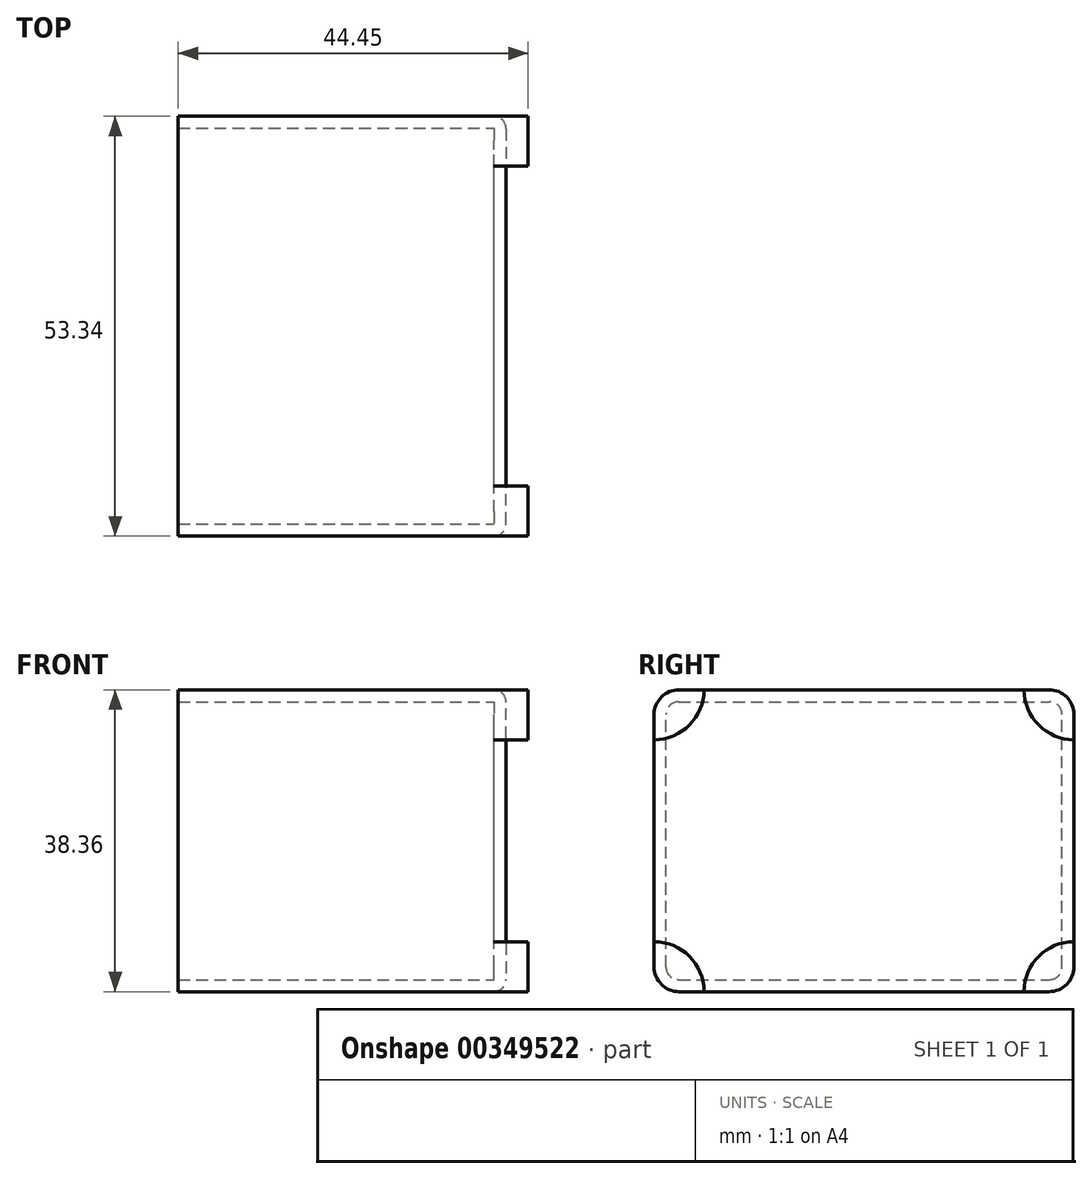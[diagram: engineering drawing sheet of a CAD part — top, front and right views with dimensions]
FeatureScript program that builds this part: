
annotation { "Feature Type Name" : "Feature", "Feature Type Description" : "" }
export const myFeature = defineFeature(function(context is Context, id is Id, definition is map)
    precondition{}
    {
        {
            var Q0;
            Q0=qCreatedBy(makeId("Right.planeOp"),FACE);
            var sketch = newSketch(context, id + "F0", { "sketchPlane" : qUnion([Q0])});
            skLineSegment(sketch, "E0.bottom", {"start": v(23.5, 19.18) * mm, "end": v(-23.5, 19.18) * mm});
            skLineSegment(sketch, "E0.top", {"start": v(23.5, -19.18) * mm, "end": v(-23.5, -19.18) * mm});
            skLineSegment(sketch, "E0.left", {"start": v(26.67, 16) * mm, "end": v(26.67, -16) * mm});
            skLineSegment(sketch, "E0.right", {"start": v(-26.67, 16) * mm, "end": v(-26.67, -16) * mm});
            skPoint(sketch, "E0.middle", {"position": v(0, 0) * mm});
            skPoint(sketch, "E1.visualSharp", {"position": v(-26.67, 19.18) * mm});
            skArc(sketch, "E1.filletArc", {"start": v(-23.5, 19.18) * mm, "mid": v(-25.74, 18.25) * mm, "end": v(-26.67, 16) * mm});
            skPoint(sketch, "E2.visualSharp", {"position": v(26.67, 19.18) * mm});
            skArc(sketch, "E2.filletArc", {"start": v(26.67, 16) * mm, "mid": v(25.74, 18.25) * mm, "end": v(23.5, 19.18) * mm});
            skPoint(sketch, "E3.visualSharp", {"position": v(26.67, -19.18) * mm});
            skArc(sketch, "E3.filletArc", {"start": v(23.5, -19.18) * mm, "mid": v(25.74, -18.25) * mm, "end": v(26.67, -16) * mm});
            skPoint(sketch, "E4.visualSharp", {"position": v(-26.67, -19.18) * mm});
            skArc(sketch, "E4.filletArc", {"start": v(-26.67, -16) * mm, "mid": v(-25.74, -18.25) * mm, "end": v(-23.5, -19.18) * mm});
            skSolve(sketch);
        }
        {
            var Q0;
            Q0 = qSketchRegion(id + "F0", true);
            extrude(context, id + "F1", {"entities" : qUnion([Q0]), "depth" : 1.52 * mm});
        }
        {
            var Q0;
            Q0=makeQuery(id+"F1.opExtrude","CAP_FACE",FACE,{"disambiguationData":[OSD([sQuery(id+"F0.wireOp",EDGE,"E0.bottom"),sQuery(id+"F0.wireOp",EDGE,"E0.top"),sQuery(id+"F0.wireOp",EDGE,"E0.left"),sQuery(id+"F0.wireOp",EDGE,"E0.right"),sQuery(id+"F0.wireOp",EDGE,"E1.filletArc"),sQuery(id+"F0.wireOp",EDGE,"E2.filletArc"),sQuery(id+"F0.wireOp",EDGE,"E3.filletArc"),sQuery(id+"F0.wireOp",EDGE,"E4.filletArc")])],"isStart":true});
            var sketch = newSketch(context, id + "F2", { "sketchPlane" : qUnion([Q0])});
            skPoint(sketch, "E5.middle", {"position": v(0, 0) * mm});
            skLineSegment(sketch, "E6.bottom", {"start": v(23.56, -17.65) * mm, "end": v(-23.56, -17.65) * mm});
            skLineSegment(sketch, "E6.top", {"start": v(23.56, 17.65) * mm, "end": v(-23.56, 17.65) * mm});
            skLineSegment(sketch, "E6.left", {"start": v(25.15, -16.07) * mm, "end": v(25.15, 16.07) * mm});
            skLineSegment(sketch, "E6.right", {"start": v(-25.15, -16.07) * mm, "end": v(-25.15, 16.07) * mm});
            skPoint(sketch, "E7.visualSharp", {"position": v(25.15, 17.65) * mm});
            skArc(sketch, "E7.filletArc", {"start": v(25.15, 16.07) * mm, "mid": v(24.68, 17.19) * mm, "end": v(23.56, 17.65) * mm});
            skPoint(sketch, "E8.visualSharp", {"position": v(25.15, -17.65) * mm});
            skArc(sketch, "E8.filletArc", {"start": v(23.56, -17.65) * mm, "mid": v(24.68, -17.19) * mm, "end": v(25.15, -16.07) * mm});
            skPoint(sketch, "E9.visualSharp", {"position": v(-25.15, -17.65) * mm});
            skArc(sketch, "E9.filletArc", {"start": v(-25.15, -16.07) * mm, "mid": v(-24.68, -17.19) * mm, "end": v(-23.56, -17.65) * mm});
            skPoint(sketch, "E10.visualSharp", {"position": v(-25.15, 17.65) * mm});
            skArc(sketch, "E10.filletArc", {"start": v(-23.56, 17.65) * mm, "mid": v(-24.68, 17.19) * mm, "end": v(-25.15, 16.07) * mm});
            skSolve(sketch);
        }
        {
            var Q0;
            Q0=makeQuery(id+"F2.imprint","IMPRINT",FACE,{"disambiguationData":[TD([[makeQuery(id+"F2.imprint","IMPRINT",EDGE,{"derivedFrom":sQuery(id+"F2.wireOp",EDGE,"E6.bottom")}),1.0]])]});
            extrude(context, id + "F3", {"entities" : qUnion([Q0]), "operationType" : NewBodyOperationType.ADD, "depth" : 40.13 * mm});
        }
        {
            var Q0;
            Q0=makeQuery(id+"F1.opExtrude","CAP_FACE",FACE,{"disambiguationData":[OSD([sQuery(id+"F0.wireOp",EDGE,"E0.bottom"),sQuery(id+"F0.wireOp",EDGE,"E0.top"),sQuery(id+"F0.wireOp",EDGE,"E0.left"),sQuery(id+"F0.wireOp",EDGE,"E0.right"),sQuery(id+"F0.wireOp",EDGE,"E1.filletArc"),sQuery(id+"F0.wireOp",EDGE,"E2.filletArc"),sQuery(id+"F0.wireOp",EDGE,"E3.filletArc"),sQuery(id+"F0.wireOp",EDGE,"E4.filletArc")])],"isStart":false});
            var sketch = newSketch(context, id + "F4", { "sketchPlane" : qUnion([Q0])});
            skLineSegment(sketch, "E11", {"start": v(-11.46, 19.18) * mm, "end": v(-32.66, 19.18) * mm, "construction": true});
            skLineSegment(sketch, "E12", {"start": v(-26.67, 6.72) * mm, "end": v(-26.67, 24.4) * mm, "construction": true});
            skCircle(sketch, "E13", {"center": v(-26.67, 19.18) * mm, "radius": 6.35 * mm});
            skSolve(sketch);
        }
        {
            var Q0;
            {var subQ5=makeQuery(id+"F1.opExtrude","CAP_EDGE",EDGE,{"disambiguationData":[OSD([sQuery(id+"F0.wireOp",EDGE,"E1.filletArc")])],"isStart":false});Q0=makeQuery(id+"F4.imprint","IMPRINT",FACE,{"disambiguationData":[TD([[makeQuery(id+"F4.imprint","IMPRINT",EDGE,{"derivedFrom":subQ5}),1.0]])]});}
            extrude(context, id + "F5", {"entities" : qUnion([Q0]), "depth" : 2.8 * mm});
        }
        {
            var Q0;
            Q0=makeQuery(id+"F5.opExtrude","SWEPT_BODY",BODY,{"disambiguationData":[OSD([sQuery(id+"F0.wireOp",EDGE,"E0.bottom"),sQuery(id+"F0.wireOp",EDGE,"E0.right"),sQuery(id+"F0.wireOp",EDGE,"E1.filletArc"),sQuery(id+"F4.wireOp",EDGE,"E13")])]});
            var Q1;
            Q1=qCreatedBy(makeId("Top.planeOp"),FACE);
            mirror(context, id + "F6", {"entities" : qUnion([Q0]), "mirrorPlane" : qUnion([Q1])});
        }
        {
            var Q0;
            Q0=makeQuery(id+"F6.opPattern","COPY",BODY,{"derivedFrom":makeQuery(id+"F5.opExtrude","SWEPT_BODY",BODY,{"disambiguationData":[OSD([sQuery(id+"F0.wireOp",EDGE,"E0.bottom"),sQuery(id+"F0.wireOp",EDGE,"E0.right"),sQuery(id+"F0.wireOp",EDGE,"E1.filletArc"),sQuery(id+"F4.wireOp",EDGE,"E13")])]}),"instanceName":"1"});
            var Q1;
            Q1=makeQuery(id+"F5.opExtrude","SWEPT_BODY",BODY,{"disambiguationData":[OSD([sQuery(id+"F0.wireOp",EDGE,"E0.bottom"),sQuery(id+"F0.wireOp",EDGE,"E0.right"),sQuery(id+"F0.wireOp",EDGE,"E1.filletArc"),sQuery(id+"F4.wireOp",EDGE,"E13")])]});
            var Q2;
            Q2=qCreatedBy(makeId("Front.planeOp"),FACE);
            mirror(context, id + "F7", {"operationType" : NewBodyOperationType.ADD, "entities" : qUnion([Q0, Q1]), "mirrorPlane" : qUnion([Q2])});
        }
        {
            var Q0;
            Q0=makeQuery(id+"F1.opExtrude","CAP_EDGE",EDGE,{"disambiguationData":[OSD([sQuery(id+"F0.wireOp",EDGE,"E0.right")])],"isStart":false});
            fillet(context, id + "F8", {"entities" : qUnion([Q0]), "radius" : 1.59 * mm, "tangentPropagation" : true, "allowEdgeOverflow" : false});
        }
        {
            var Q0;
            Q0=makeQuery(id+"F1.opExtrude","CAP_EDGE",EDGE,{"disambiguationData":[OSD([sQuery(id+"F0.wireOp",EDGE,"E0.top")])],"isStart":false});
            fillet(context, id + "F9", {"entities" : qUnion([Q0]), "radius" : 1.59 * mm, "tangentPropagation" : true, "allowEdgeOverflow" : false});
        }
        {
            var Q0;
            Q0=makeQuery(id+"F1.opExtrude","CAP_EDGE",EDGE,{"disambiguationData":[OSD([sQuery(id+"F0.wireOp",EDGE,"E0.left")])],"isStart":false});
            fillet(context, id + "F10", {"entities" : qUnion([Q0]), "radius" : 1.59 * mm, "tangentPropagation" : true, "allowEdgeOverflow" : false});
        }
        {
            var Q0;
            Q0=makeQuery(id+"F1.opExtrude","CAP_EDGE",EDGE,{"disambiguationData":[OSD([sQuery(id+"F0.wireOp",EDGE,"E0.bottom")])],"isStart":false});
            fillet(context, id + "F11", {"entities" : qUnion([Q0]), "radius" : 1.59 * mm, "tangentPropagation" : true, "allowEdgeOverflow" : false});
        }
    });
